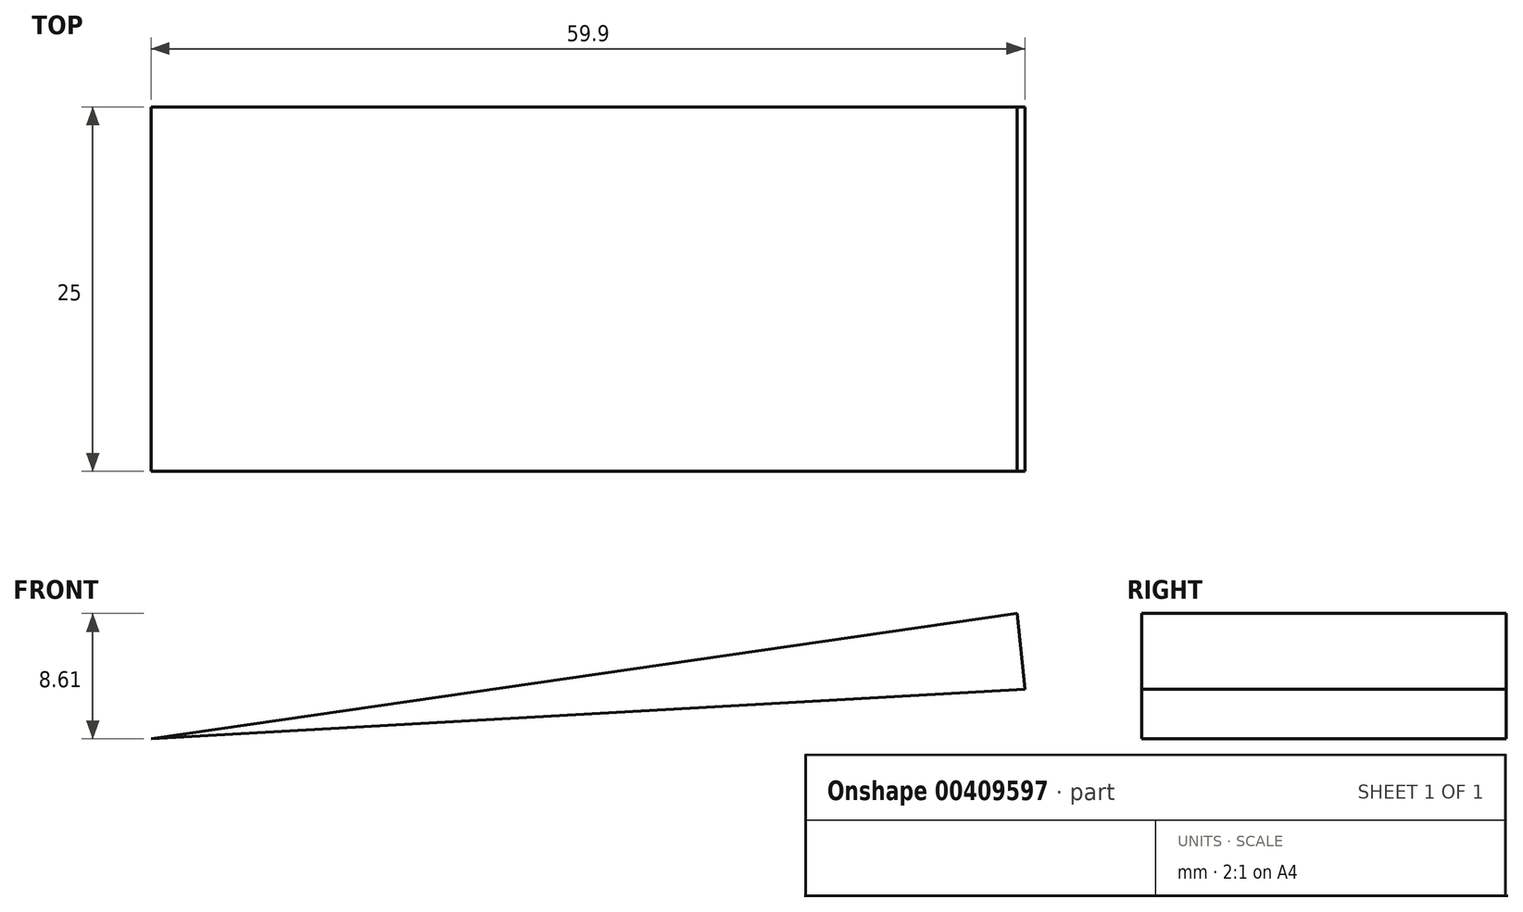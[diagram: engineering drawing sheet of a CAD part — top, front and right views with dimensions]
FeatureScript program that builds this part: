
annotation { "Feature Type Name" : "Feature", "Feature Type Description" : "" }
export const myFeature = defineFeature(function(context is Context, id is Id, definition is map)
    precondition{}
    {
        {
            var Q0;
            Q0=qCreatedBy(makeId("Front.planeOp"),FACE);
            var sketch = newSketch(context, id + "F0", { "sketchPlane" : qUnion([Q0])});
            skLineSegment(sketch, "E0", {"start": v(-20.02, 0) * mm, "end": v(39.36, 8.6) * mm});
            skLineSegment(sketch, "E1", {"start": v(-20.02, 0) * mm, "end": v(39.88, 3.4) * mm});
            skLineSegment(sketch, "E2", {"start": v(39.36, 8.6) * mm, "end": v(39.88, 3.4) * mm});
            skSolve(sketch);
        }
        {
            var Q0;
            Q0=makeQuery(id+"F0.imprint","IMPRINT",FACE,{"disambiguationData":[TD([[makeQuery(id+"F0.imprint","IMPRINT",EDGE,{"derivedFrom":sQuery(id+"F0.wireOp",EDGE,"E0")}),-1.0]])]});
            extrude(context, id + "F1", {"entities" : qUnion([Q0]), "endBound" : BoundingType.SYMMETRIC, "depth" : 25 * mm});
        }
    });
